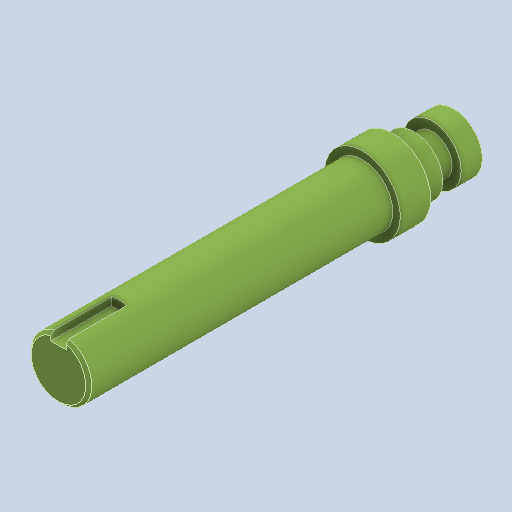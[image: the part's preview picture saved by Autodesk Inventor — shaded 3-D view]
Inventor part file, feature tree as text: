
AUTODESK INVENTOR PART (.ipt)
format: ipt  version: 2022 (Build 260153000, 153)  size: 147,456 bytes
history: native  units: in
note: dims shown in document units (in); Inventor stores cm internally (conversion verified against a paired STEP export)
features: extrude x6, sketch x6, chamfer x1
ambient origin geometry x8: Origin, YZ Plane, XZ Plane, XY Plane, X Axis, Y Axis, Z Axis, Center Point
bodies: Solid1 (feature_tree)
feature tree (13):
  extrude  "Extrusion1"  Depth=0.2756in TaperAngle=0.0deg
  extrude  "Extrusion2"  Depth=0.2362in TaperAngle=0.0deg
  extrude  "Extrusion3"  Depth=0.2756in TaperAngle=0.0deg
  extrude  "Extrusion4"  Depth=0.3937in TaperAngle=0.0deg
  extrude  "Extrusion5"  Depth=0.7874in TaperAngle=0.0deg
  chamfer  "Chamfer1"  Distance=0.0394in Angle=45.0deg
  extrude  "Extrusion6"  Depth=0.1969in
  sketch  "Sketch1"  dims[d0=0.748in d1=0.2756in d2=0.0in]
  sketch  "Sketch2"  dims[d3=0.5118in d4=0.2362in d5=0.0in]
  sketch  "Sketch3"  dims[d6=0.748in d7=0.2756in d8=0.0in]
  sketch  "Sketch4"  dims[d9=0.9843in d10=0.3937in d11=0.0in]
  sketch  "Sketch5"  dims[d12=0.7874in d13=3.937in d14=0.0in d15=0.0394in d16=0.0787in d17=45.0deg]
  sketch  "Sketch6"  dims[d18=0.1969in d19=0.1969in d20=0.2756in d21=0.7874in d22=0.0in]
